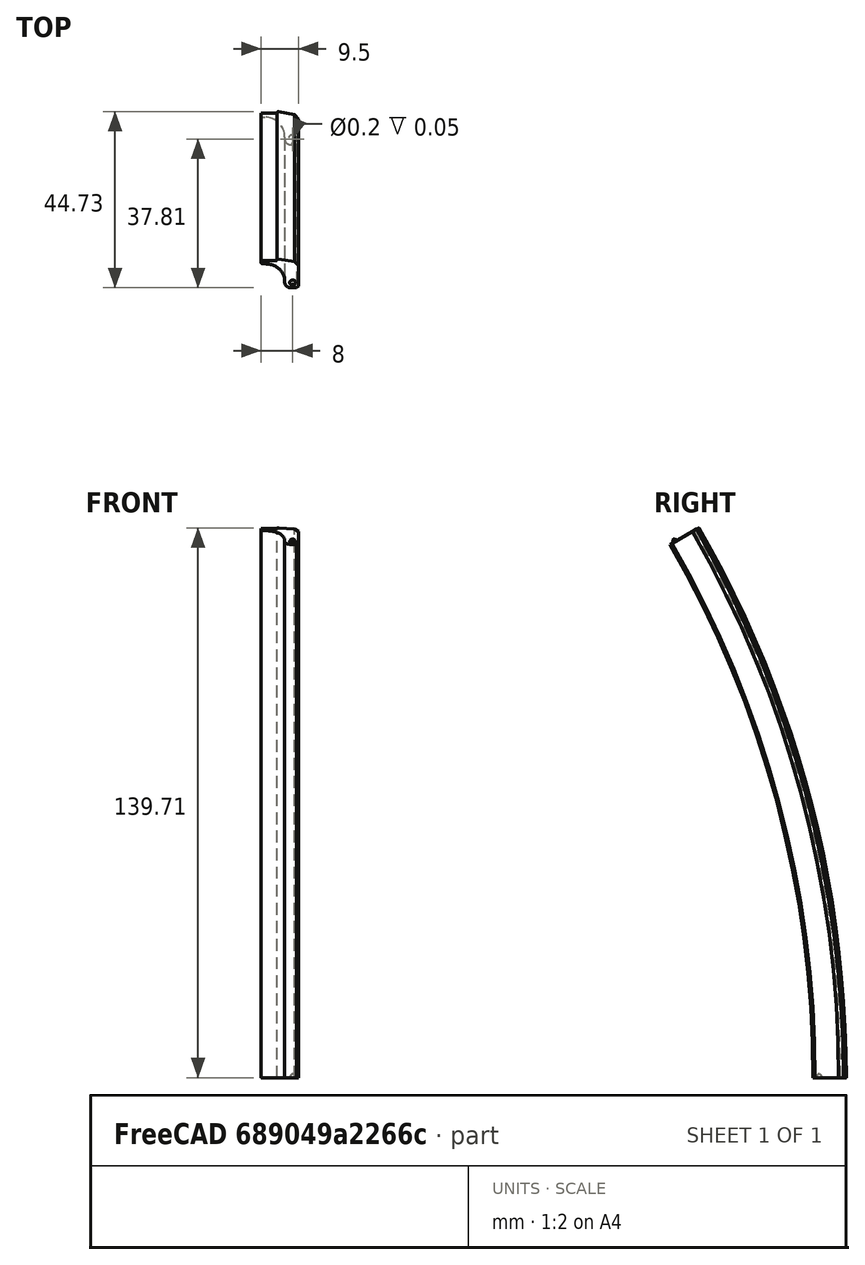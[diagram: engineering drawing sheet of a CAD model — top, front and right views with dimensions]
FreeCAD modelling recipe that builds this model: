
FCSTD DOCUMENT  (FreeCAD 0.16R)
Label: BeadBlock1.1
License: All rights reserved
LicenseURL: http://en.wikipedia.org/wiki/All_rights_reserved
objects: PartDesign::Fillet×4, PartDesign::Chamfer×4, Sketcher::SketchObject×3, PartDesign::Revolution×1, PartDesign::Pad×1, PartDesign::Pocket×1, Mesh::Feature×1
note: 17 computed .brp shape members not serialized (recipe doc carries the construction recipe); baked Part::Feature solids carry a one-line shape summary decoded from their .brp

FEATURE [Sketcher::SketchObject] Sketch
  sketch-geometry (8):
    g0: LineSegment StartX=0 StartY=279 StartZ=0 EndX=4 EndY=279 EndZ=0
    g1: LineSegment StartX=4 StartY=279 StartZ=0 EndX=4 EndY=279.5 EndZ=0
    g2: LineSegment StartX=0 StartY=278 StartZ=0 EndX=0 EndY=279 EndZ=0
    g3: LineSegment StartX=0 StartY=278 StartZ=0 EndX=6 EndY=278 EndZ=0
    g4: LineSegment StartX=6 StartY=278 StartZ=0 EndX=6 EndY=271 EndZ=0
    g5: LineSegment StartX=6 StartY=271 StartZ=0 EndX=9.5 EndY=271 EndZ=0
    g6: LineSegment StartX=9.5 StartY=271 StartZ=0 EndX=9.5 EndY=278.5 EndZ=0
    g7: LineSegment StartX=4 StartY=279.5 StartZ=0 EndX=9.5 EndY=278.5 EndZ=0
  constraints (24):
    c: Horizontal(g0)
    c: PointOnObject(g0,g-2)
    c: DistanceY(g0) = 279
    c: Distance(g0) = 4
    c: Coincident(g1,g0)
    c: Vertical(g1)
    c: Distance(g1) = 0.5
    c: Vertical(g2)
    c: Coincident(g2,g0)
    c: Distance(g2) = 1
    c: Horizontal(g3)
    c: Coincident(g3,g2)
    c: Distance(g3) = 6
    c: Vertical(g4)
    c: Coincident(g4,g3)
    c: Distance(g4) = 7
    c: Horizontal(g5)
    c: Coincident(g5,g4)
    c: Distance(g5) = 3.5
    c: Vertical(g6)
    c: Coincident(g5,g6)
    c: Distance(g6) = 7.5
    c: Coincident(g7,g1)
    c: Coincident(g7,g6)
FEATURE [PartDesign::Revolution] Revolution
  Angle = 30
  Axis = (1,0,0)
  Base = (0,0,0)
  ReferenceAxis = -> Sketch [H_Axis]
  Sketch = -> Sketch
FEATURE [PartDesign::Fillet] Fillet
  Base = -> Revolution [Edge17]
  Radius = 5
FEATURE [PartDesign::Fillet] Fillet001
  Base = -> Fillet [Edge26]
  Radius = 0.4
FEATURE [PartDesign::Fillet] Fillet002
  Base = -> Fillet001 [Edge20]
  Radius = 1.5
FEATURE [PartDesign::Fillet] Fillet003
  Base = -> Fillet002 [Edge27]
  Radius = 0.3
FEATURE [PartDesign::Chamfer] Chamfer
  Base = -> Fillet003 [Edge30]
  Size = 0.5
FEATURE [PartDesign::Chamfer] Chamfer001
  Base = -> Chamfer [Edge21]
  Size = 1
FEATURE [Sketcher::SketchObject] Sketch001
  ExternalGeometry = -> [Chamfer001]
  Placement = pos=(0,0,0) rot=(1,0,0;0.523599rad)
  Support = -> Chamfer001 [Face16]
  sketch-geometry (1):
    g0: Circle CenterX=8 CenterY=272.5 CenterZ=0 NormalX=0 NormalY=0 NormalZ=1 Radius=0.75
  constraints (3):
    c: Radius(g0) = 0.75
    c: Distance(g0,g-3) = 1.5
    c: Distance(g0,g-4) = 1.5
FEATURE [PartDesign::Pad] Pad
  Length = 0.75
  Length2 = 100
  Sketch = -> Sketch001
  Type = 0
FEATURE [PartDesign::Chamfer] Chamfer002
  Base = -> Pad [Edge1]
  Size = 0.72
FEATURE [Sketcher::SketchObject] Sketch002
  ExternalGeometry = -> [Chamfer002]
  Placement = pos=(0,0,0) rot=(1,0,0;3.14159rad)
  Support = -> Chamfer002 [Face19]
  sketch-geometry (1):
    g0: Circle CenterX=8 CenterY=-272.5 CenterZ=0 NormalX=0 NormalY=0 NormalZ=1 Radius=0.1
  constraints (3):
    c: Distance(g0,g-4) = 1.5
    c: Distance(g0,g-3) = 1.5
    c: Radius(g0) = 0.1
FEATURE [PartDesign::Pocket] Pocket
  Length = 1
  Sketch = -> Sketch002
  Type = 0
FEATURE [PartDesign::Chamfer] Chamfer003
  Base = -> Pocket [Edge48]
  Size = 0.95
FEATURE [Mesh::Feature] Mesh  label="Chamfer003 (Meshed)"
